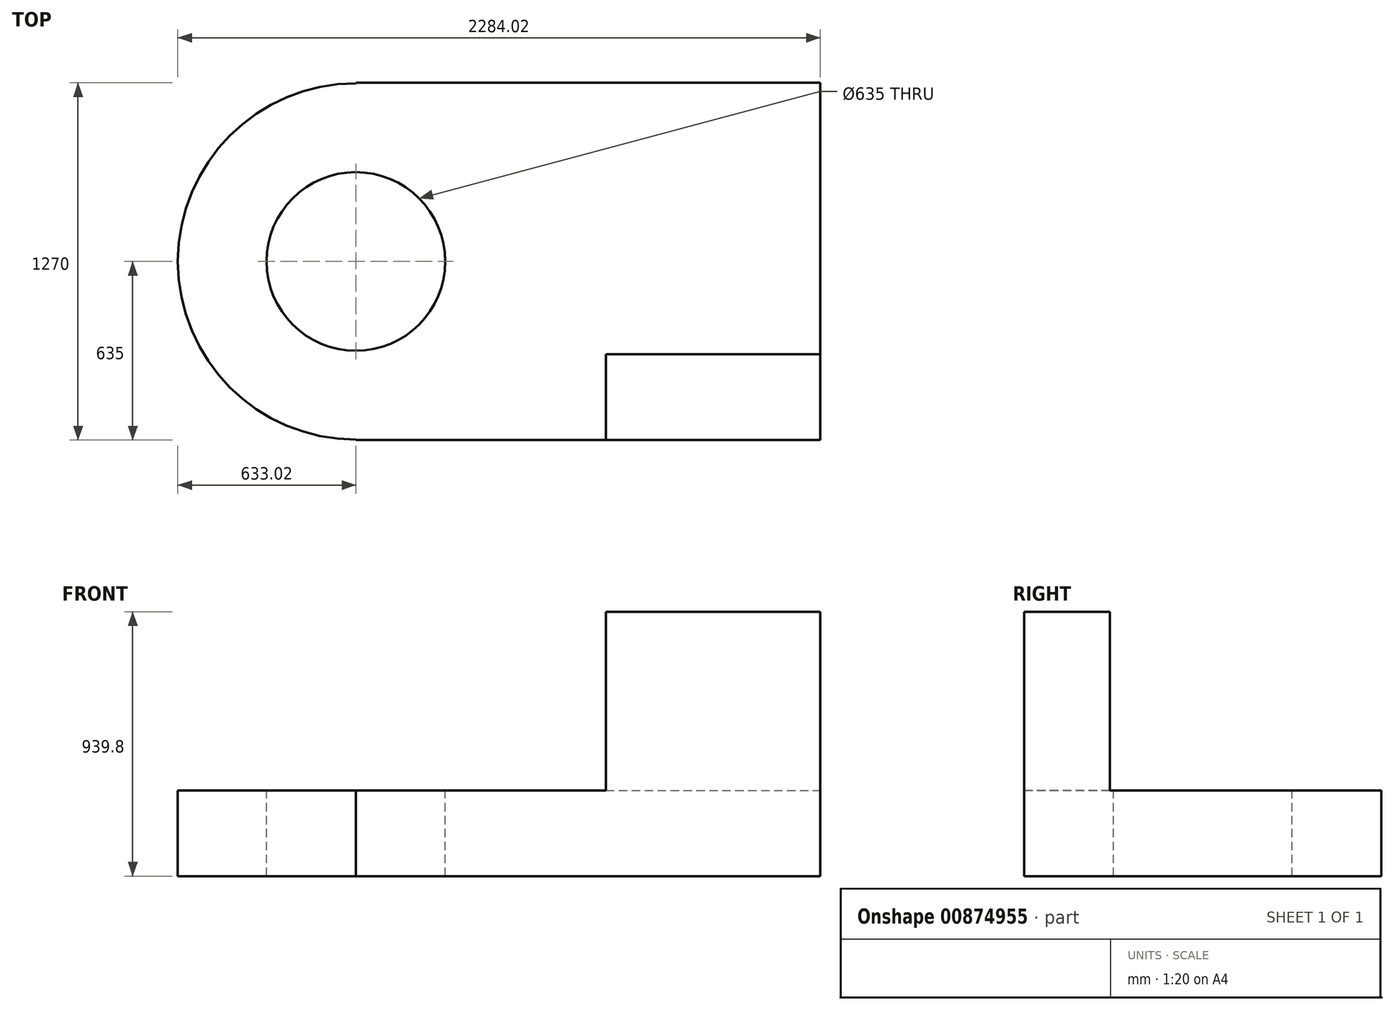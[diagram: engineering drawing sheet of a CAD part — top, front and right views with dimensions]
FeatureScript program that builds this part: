
annotation { "Feature Type Name" : "Feature", "Feature Type Description" : "" }
export const myFeature = defineFeature(function(context is Context, id is Id, definition is map)
    precondition{}
    {
        {
            var Q0;
            Q0=qCreatedBy(makeId("Top.planeOp"),FACE);
            var sketch = newSketch(context, id + "F0", { "sketchPlane" : qUnion([Q0])});
            skLineSegment(sketch, "E0", {"start": v(0, 0) * mm, "end": v(0, 1270) * mm});
            skLineSegment(sketch, "E1", {"start": v(0, 1270) * mm, "end": v(-1651, 1270) * mm});
            skLineSegment(sketch, "E2", {"start": v(0, 0) * mm, "end": v(-1651, 0) * mm});
            skLineSegment(sketch, "E3", {"start": v(-1651, 0) * mm, "end": v(-1651, 1270) * mm});
            skCircle(sketch, "E4", {"center": v(-1651, 635) * mm, "radius": 633.02 * mm});
            skSolve(sketch);
        }
        {
            var Q0;
            Q0 = qSketchRegion(id + "F0", true);
            extrude(context, id + "F1", {"entities" : qUnion([Q0]), "depth" : 304.8 * mm, "offsetDistance" : 25.4 * mm});
        }
        {
            var Q0;
            Q0=makeQuery(id+"F1.opExtrude","CAP_FACE",FACE,{"disambiguationData":[OSD([sQuery(id+"F0.wireOp",EDGE,"E0"),sQuery(id+"F0.wireOp",EDGE,"E1"),sQuery(id+"F0.wireOp",EDGE,"E2"),sQuery(id+"F0.wireOp",EDGE,"E3"),sQuery(id+"F0.wireOp",EDGE,"E4")])],"isStart":false});
            var sketch = newSketch(context, id + "F2", { "sketchPlane" : qUnion([Q0])});
            skLineSegment(sketch, "E5", {"start": v(0, 0) * mm, "end": v(-1651, 1.98) * mm});
            skLineSegment(sketch, "E6", {"start": v(0, 1270) * mm, "end": v(-1651, 1270) * mm});
            skLineSegment(sketch, "E7", {"start": v(-1651, 1270) * mm, "end": v(-1651, 0) * mm});
            skCircle(sketch, "E8", {"center": v(-1651, 635) * mm, "radius": 317.5 * mm});
            skSolve(sketch);
        }
        {
            var Q0;
            Q0 = qSketchRegion(id + "F2", true);
            extrude(context, id + "F3", {"entities" : qUnion([Q0]), "operationType" : NewBodyOperationType.REMOVE, "oppositeDirection" : true, "depth" : 2540 * mm, "offsetDistance" : 25.4 * mm});
        }
        {
            var Q0;
            Q0=makeQuery(id+"F1.opExtrude","CAP_FACE",FACE,{"disambiguationData":[OSD([sQuery(id+"F0.wireOp",EDGE,"E0"),sQuery(id+"F0.wireOp",EDGE,"E1"),sQuery(id+"F0.wireOp",EDGE,"E2"),sQuery(id+"F0.wireOp",EDGE,"E3"),sQuery(id+"F0.wireOp",EDGE,"E4")])],"isStart":false});
            var sketch = newSketch(context, id + "F4", { "sketchPlane" : qUnion([Q0])});
            skLineSegment(sketch, "E9", {"start": v(0, 0) * mm, "end": v(-762, 0) * mm});
            skLineSegment(sketch, "E10", {"start": v(-762, 0) * mm, "end": v(-762, 304.8) * mm});
            skLineSegment(sketch, "E11", {"start": v(-762, 304.8) * mm, "end": v(0, 304.8) * mm});
            skLineSegment(sketch, "E12", {"start": v(0, 304.8) * mm, "end": v(0, 0) * mm});
            skSolve(sketch);
        }
        {
            var Q0;
            Q0=makeQuery(id+"F4.imprint","IMPRINT",FACE,{"disambiguationData":[TD([[makeQuery(id+"F4.imprint","IMPRINT",EDGE,{"derivedFrom":sQuery(id+"F4.wireOp",EDGE,"E9")}),-1.0]])]});
            extrude(context, id + "F5", {"entities" : qUnion([Q0]), "operationType" : NewBodyOperationType.ADD, "depth" : 635 * mm, "offsetDistance" : 25.4 * mm});
        }
    });
